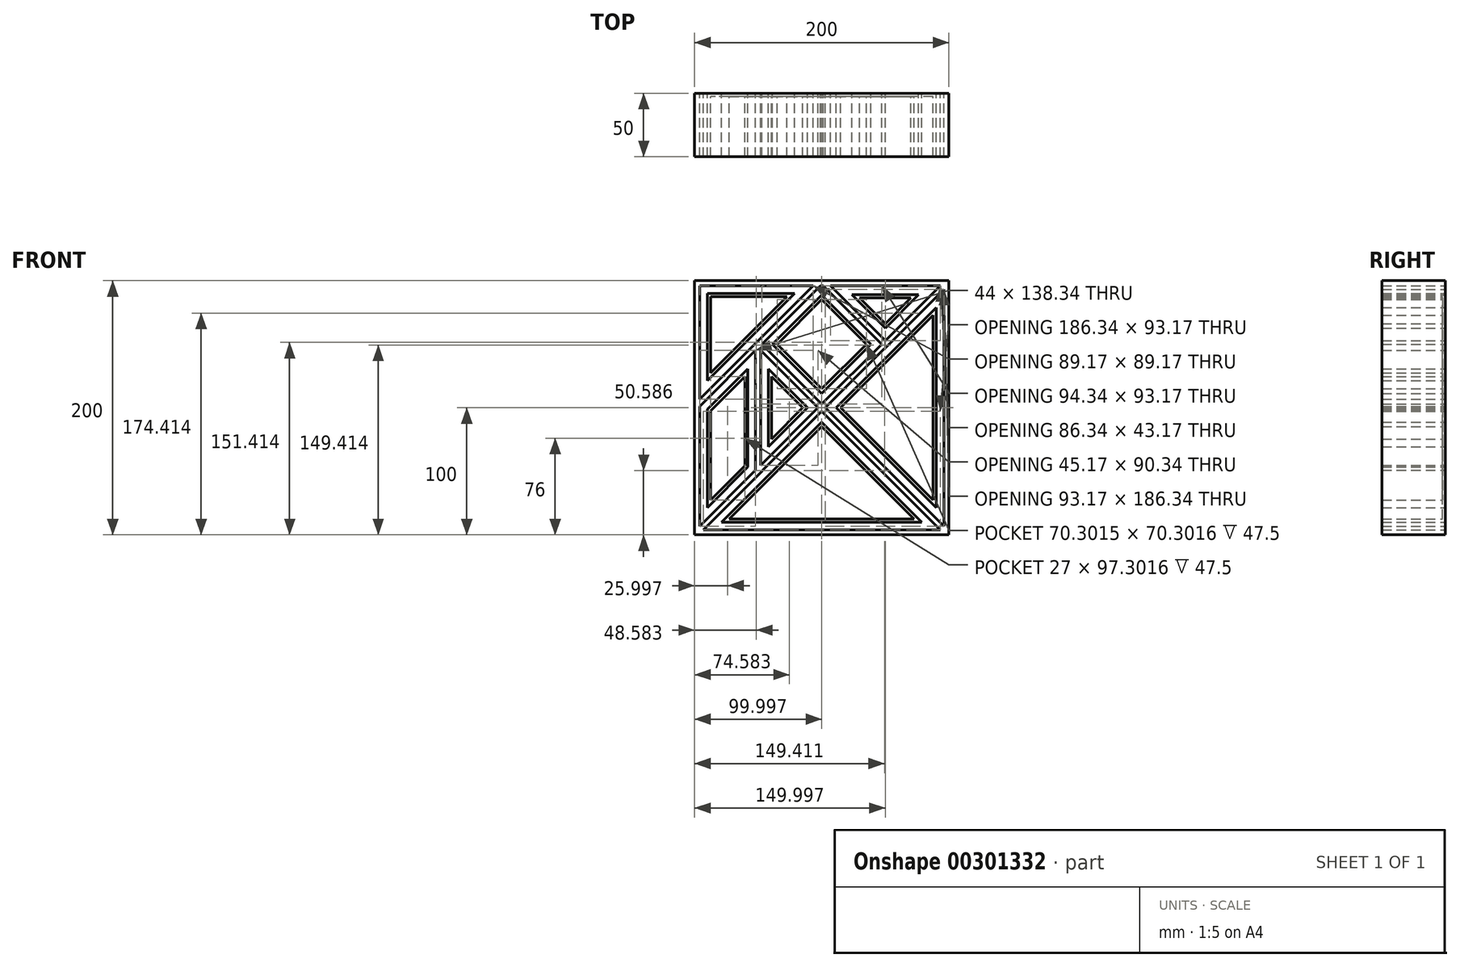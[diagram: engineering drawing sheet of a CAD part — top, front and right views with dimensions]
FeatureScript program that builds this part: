
annotation { "Feature Type Name" : "Feature", "Feature Type Description" : "" }
export const myFeature = defineFeature(function(context is Context, id is Id, definition is map)
    precondition{}
    {
        {
            var Q0;
            Q0=qCreatedBy(makeId("Front.planeOp"),FACE);
            var sketch = newSketch(context, id + "F0", { "sketchPlane" : qUnion([Q0])});
            skLineSegment(sketch, "E0.bottom", {"start": v(-112.27, 100) * mm, "end": v(87.73, 100) * mm});
            skLineSegment(sketch, "E0.top", {"start": v(-112.27, -100) * mm, "end": v(87.73, -100) * mm});
            skLineSegment(sketch, "E0.left", {"start": v(-112.27, 100) * mm, "end": v(-112.27, -100) * mm});
            skLineSegment(sketch, "E0.right", {"start": v(87.73, 100) * mm, "end": v(87.73, -100) * mm});
            skLineSegment(sketch, "E1", {"start": v(87.73, 100) * mm, "end": v(-108.27, -96) * mm, "construction": true});
            skLineSegment(sketch, "E2", {"start": v(-12.27, 100) * mm, "end": v(-112.27, 0) * mm, "construction": true});
            skLineSegment(sketch, "E3", {"start": v(-62.27, 50) * mm, "end": v(-62.27, -50) * mm, "construction": true});
            skLineSegment(sketch, "E4", {"start": v(-62.27, 50) * mm, "end": v(-12.27, 0) * mm, "construction": true});
            skPoint(sketch, "E4.endSnap0", {"position": v(-12.27, 0) * mm});
            skLineSegment(sketch, "E5", {"start": v(-12.27, 0) * mm, "end": v(83.73, -96) * mm, "construction": true});
            skLineSegment(sketch, "E6", {"start": v(-12.27, 100) * mm, "end": v(37.73, 50) * mm, "construction": true});
            skLineSegment(sketch, "E7.bottom", {"start": v(80.9, -96) * mm, "end": v(-105.44, -96) * mm});
            skLineSegment(sketch, "E7.top", {"start": v(80.9, 96) * mm, "end": v(-5.44, 96) * mm});
            skLineSegment(sketch, "E7.left", {"start": v(83.73, -93.17) * mm, "end": v(83.73, 93.17) * mm});
            skLineSegment(sketch, "E7.right", {"start": v(-108.27, -93.17) * mm, "end": v(-108.27, 1.17) * mm});
            skLineSegment(sketch, "E8", {"start": v(-19.1, 96) * mm, "end": v(-108.27, 6.83) * mm});
            skLineSegment(sketch, "E9", {"start": v(-108.27, 1.17) * mm, "end": v(-64.27, 45.17) * mm});
            skLineSegment(sketch, "E10", {"start": v(-64.27, 45.17) * mm, "end": v(-64.27, -49.17) * mm});
            skLineSegment(sketch, "E11", {"start": v(-64.27, -49.17) * mm, "end": v(-108.27, -93.17) * mm});
            skLineSegment(sketch, "E12", {"start": v(-105.44, -96) * mm, "end": v(-12.27, -2.83) * mm});
            skLineSegment(sketch, "E13", {"start": v(-12.27, -2.83) * mm, "end": v(80.9, -96) * mm});
            skLineSegment(sketch, "E14", {"start": v(83.73, 93.17) * mm, "end": v(-9.44, 0) * mm});
            skLineSegment(sketch, "E15", {"start": v(-9.44, 0) * mm, "end": v(83.73, -93.17) * mm});
            skLineSegment(sketch, "E16", {"start": v(-60.27, 45.17) * mm, "end": v(-60.27, -45.17) * mm});
            skLineSegment(sketch, "E17", {"start": v(-60.27, -45.17) * mm, "end": v(-15.1, 0) * mm});
            skLineSegment(sketch, "E18", {"start": v(-15.1, 0) * mm, "end": v(-60.27, 45.17) * mm});
            skLineSegment(sketch, "E19", {"start": v(-5.44, 96) * mm, "end": v(37.73, 52.83) * mm});
            skLineSegment(sketch, "E20", {"start": v(37.73, 52.83) * mm, "end": v(80.9, 96) * mm});
            skLineSegment(sketch, "E21", {"start": v(-13.44, 96) * mm, "end": v(-59.44, 50) * mm});
            skLineSegment(sketch, "E22", {"start": v(-59.44, 50) * mm, "end": v(-12.27, 2.83) * mm});
            skLineSegment(sketch, "E23", {"start": v(-12.27, 2.83) * mm, "end": v(34.9, 50) * mm});
            skLineSegment(sketch, "E24", {"start": v(34.9, 50) * mm, "end": v(-11.1, 96) * mm});
            skPoint(sketch, "E25.orphan", {"position": v(83.73, 96) * mm});
            skLineSegment(sketch, "E26.trimOffspring", {"start": v(-11.1, 96) * mm, "end": v(-13.44, 96) * mm});
            skLineSegment(sketch, "E27.trimOffspring", {"start": v(-19.1, 96) * mm, "end": v(-108.27, 96) * mm});
            skLineSegment(sketch, "E28.trimOffspring", {"start": v(-108.27, 6.83) * mm, "end": v(-108.27, 96) * mm});
            skPoint(sketch, "E29.orphan", {"position": v(-108.27, -96) * mm});
            skSolve(sketch);
        }
        {
            var Q0;
            Q0 = qSketchRegion(id + "F0", true);
            extrude(context, id + "F1", {"entities" : qUnion([Q0]), "depth" : 50 * mm});
        }
        {
            var Q0;
            Q0=qCreatedBy(makeId("Front.planeOp"),FACE);
            var sketch = newSketch(context, id + "F2", { "sketchPlane" : qUnion([Q0])});
            skLineSegment(sketch, "E30.0", {"start": v(81.73, 88.34) * mm, "end": v(-6.62, 0) * mm});
            skLineSegment(sketch, "E30.1", {"start": v(81.73, -88.34) * mm, "end": v(81.73, 88.34) * mm});
            skLineSegment(sketch, "E30.2", {"start": v(-6.62, 0) * mm, "end": v(81.73, -88.34) * mm});
            skLineSegment(sketch, "E31.0", {"start": v(77.73, 78.69) * mm, "end": v(-0.96, 0) * mm});
            skLineSegment(sketch, "E31.1", {"start": v(77.73, -78.69) * mm, "end": v(77.73, 78.69) * mm});
            skLineSegment(sketch, "E31.2", {"start": v(-0.96, 0) * mm, "end": v(77.73, -78.69) * mm});
            skLineSegment(sketch, "E32.0", {"start": v(-0.62, 94) * mm, "end": v(37.73, 55.66) * mm});
            skLineSegment(sketch, "E32.1", {"start": v(76.07, 94) * mm, "end": v(-0.62, 94) * mm});
            skLineSegment(sketch, "E32.2", {"start": v(37.73, 55.66) * mm, "end": v(76.07, 94) * mm});
            skLineSegment(sketch, "E33.0", {"start": v(11.46, 89) * mm, "end": v(37.73, 62.73) * mm});
            skLineSegment(sketch, "E33.1", {"start": v(64, 89) * mm, "end": v(11.46, 89) * mm});
            skLineSegment(sketch, "E33.2", {"start": v(37.73, 62.73) * mm, "end": v(64, 89) * mm});
            skLineSegment(sketch, "E34.0", {"start": v(-100.62, -94) * mm, "end": v(-12.27, -5.66) * mm});
            skLineSegment(sketch, "E34.1", {"start": v(76.07, -94) * mm, "end": v(-100.62, -94) * mm});
            skLineSegment(sketch, "E34.2", {"start": v(-12.27, -5.66) * mm, "end": v(76.07, -94) * mm});
            skLineSegment(sketch, "E35.0", {"start": v(-90.96, -90) * mm, "end": v(-12.27, -11.31) * mm});
            skLineSegment(sketch, "E35.1", {"start": v(66.41, -90) * mm, "end": v(-90.96, -90) * mm});
            skLineSegment(sketch, "E35.2", {"start": v(-12.27, -11.31) * mm, "end": v(66.41, -90) * mm});
            skLineSegment(sketch, "E36.0", {"start": v(-106.27, 0.34) * mm, "end": v(-66.27, 40.34) * mm});
            skLineSegment(sketch, "E36.1", {"start": v(-106.27, -88.34) * mm, "end": v(-106.27, 0.34) * mm});
            skLineSegment(sketch, "E36.2", {"start": v(-66.27, -48.34) * mm, "end": v(-106.27, -88.34) * mm});
            skLineSegment(sketch, "E36.3", {"start": v(-66.27, 40.34) * mm, "end": v(-66.27, -48.34) * mm});
            skLineSegment(sketch, "E37.0", {"start": v(-102.27, -78.69) * mm, "end": v(-102.27, -1.31) * mm});
            skLineSegment(sketch, "E37.1", {"start": v(-70.27, -46.69) * mm, "end": v(-102.27, -78.69) * mm});
            skLineSegment(sketch, "E37.2", {"start": v(-70.27, 30.69) * mm, "end": v(-70.27, -46.69) * mm});
            skLineSegment(sketch, "E37.3", {"start": v(-102.27, -1.31) * mm, "end": v(-70.27, 30.69) * mm});
            skLineSegment(sketch, "E38.0", {"start": v(-23.93, 94) * mm, "end": v(-106.27, 11.66) * mm});
            skLineSegment(sketch, "E38.1", {"start": v(-23.93, 94) * mm, "end": v(-106.27, 94) * mm});
            skLineSegment(sketch, "E38.2", {"start": v(-106.27, 11.66) * mm, "end": v(-106.27, 94) * mm});
            skLineSegment(sketch, "E39.0", {"start": v(-102.27, 21.31) * mm, "end": v(-102.27, 90) * mm});
            skLineSegment(sketch, "E39.1", {"start": v(-33.59, 90) * mm, "end": v(-102.27, 21.31) * mm});
            skLineSegment(sketch, "E39.2", {"start": v(-33.59, 90) * mm, "end": v(-102.27, 90) * mm});
            skLineSegment(sketch, "E40.0", {"start": v(-58.27, 40.34) * mm, "end": v(-58.27, -40.34) * mm});
            skLineSegment(sketch, "E40.1", {"start": v(-17.93, 0) * mm, "end": v(-58.27, 40.34) * mm});
            skLineSegment(sketch, "E40.2", {"start": v(-58.27, -40.34) * mm, "end": v(-17.93, 0) * mm});
            skLineSegment(sketch, "E41.0", {"start": v(-54.27, 30.69) * mm, "end": v(-54.27, -30.69) * mm});
            skLineSegment(sketch, "E41.1", {"start": v(-23.59, 0) * mm, "end": v(-54.27, 30.69) * mm});
            skLineSegment(sketch, "E41.2", {"start": v(-54.27, -30.69) * mm, "end": v(-23.59, 0) * mm});
            skLineSegment(sketch, "E42.0", {"start": v(32.07, 50) * mm, "end": v(-12.27, 94.34) * mm});
            skLineSegment(sketch, "E42.1", {"start": v(-12.27, 5.66) * mm, "end": v(32.07, 50) * mm});
            skLineSegment(sketch, "E42.2", {"start": v(-56.62, 50) * mm, "end": v(-12.27, 5.66) * mm});
            skLineSegment(sketch, "E42.3", {"start": v(-12.27, 94.34) * mm, "end": v(-56.62, 50) * mm});
            skLineSegment(sketch, "E43.0", {"start": v(-12.27, 88.69) * mm, "end": v(-50.96, 50) * mm});
            skLineSegment(sketch, "E43.1", {"start": v(26.41, 50) * mm, "end": v(-12.27, 88.69) * mm});
            skLineSegment(sketch, "E43.2", {"start": v(-12.27, 11.31) * mm, "end": v(26.41, 50) * mm});
            skLineSegment(sketch, "E43.3", {"start": v(-50.96, 50) * mm, "end": v(-12.27, 11.31) * mm});
            skSolve(sketch);
        }
        {
            var Q0;
            Q0=makeQuery(id+"F2.imprint","IMPRINT",FACE,{"disambiguationData":[TD([[makeQuery(id+"F2.imprint","IMPRINT",EDGE,{"derivedFrom":sQuery(id+"F2.wireOp",EDGE,"E31.0")}),1.0]])]});
            var Q1;
            Q1=makeQuery(id+"F2.imprint","IMPRINT",FACE,{"disambiguationData":[TD([[makeQuery(id+"F2.imprint","IMPRINT",EDGE,{"derivedFrom":sQuery(id+"F2.wireOp",EDGE,"E35.0")}),-1.0]])]});
            var Q2;
            Q2=makeQuery(id+"F2.imprint","IMPRINT",FACE,{"disambiguationData":[TD([[makeQuery(id+"F2.imprint","IMPRINT",EDGE,{"derivedFrom":sQuery(id+"F2.wireOp",EDGE,"E43.0")}),1.0]])]});
            var Q3;
            Q3=makeQuery(id+"F2.imprint","IMPRINT",FACE,{"disambiguationData":[TD([[makeQuery(id+"F2.imprint","IMPRINT",EDGE,{"derivedFrom":sQuery(id+"F2.wireOp",EDGE,"E41.0")}),1.0]])]});
            var Q4;
            Q4=makeQuery(id+"F2.imprint","IMPRINT",FACE,{"disambiguationData":[TD([[makeQuery(id+"F2.imprint","IMPRINT",EDGE,{"derivedFrom":sQuery(id+"F2.wireOp",EDGE,"E37.0")}),-1.0]])]});
            var Q5;
            Q5=makeQuery(id+"F2.imprint","IMPRINT",FACE,{"disambiguationData":[TD([[makeQuery(id+"F2.imprint","IMPRINT",EDGE,{"derivedFrom":sQuery(id+"F2.wireOp",EDGE,"E39.0")}),-1.0]])]});
            var Q6;
            Q6=makeQuery(id+"F2.imprint","IMPRINT",FACE,{"disambiguationData":[TD([[makeQuery(id+"F2.imprint","IMPRINT",EDGE,{"derivedFrom":sQuery(id+"F2.wireOp",EDGE,"E33.0")}),1.0]])]});
            extrude(context, id + "F3", {"entities" : qUnion([Q0, Q1, Q2, Q3, Q4, Q5, Q6]), "depth" : 50 * mm});
        }
        {
            var Q0;
            Q0=makeQuery(id+"F3.opExtrude","CAP_FACE",FACE,{"disambiguationData":[OSD([sQuery(id+"F2.wireOp",EDGE,"E37.0"),sQuery(id+"F2.wireOp",EDGE,"E37.1"),sQuery(id+"F2.wireOp",EDGE,"E37.2"),sQuery(id+"F2.wireOp",EDGE,"E37.3")])],"isStart":false});
            var Q1;
            Q1=makeQuery(id+"F3.opExtrude","CAP_FACE",FACE,{"disambiguationData":[OSD([sQuery(id+"F2.wireOp",EDGE,"E39.0"),sQuery(id+"F2.wireOp",EDGE,"E39.1"),sQuery(id+"F2.wireOp",EDGE,"E39.2")])],"isStart":false});
            var Q2;
            Q2=makeQuery(id+"F3.opExtrude","CAP_FACE",FACE,{"disambiguationData":[OSD([sQuery(id+"F2.wireOp",EDGE,"E35.0"),sQuery(id+"F2.wireOp",EDGE,"E35.1"),sQuery(id+"F2.wireOp",EDGE,"E35.2")])],"isStart":false});
            var Q3;
            Q3=makeQuery(id+"F3.opExtrude","CAP_FACE",FACE,{"disambiguationData":[OSD([sQuery(id+"F2.wireOp",EDGE,"E41.0"),sQuery(id+"F2.wireOp",EDGE,"E41.1"),sQuery(id+"F2.wireOp",EDGE,"E41.2")])],"isStart":false});
            var Q4;
            Q4=makeQuery(id+"F3.opExtrude","CAP_FACE",FACE,{"disambiguationData":[OSD([sQuery(id+"F2.wireOp",EDGE,"E43.0"),sQuery(id+"F2.wireOp",EDGE,"E43.1"),sQuery(id+"F2.wireOp",EDGE,"E43.2"),sQuery(id+"F2.wireOp",EDGE,"E43.3")])],"isStart":false});
            var Q5;
            Q5=makeQuery(id+"F3.opExtrude","CAP_FACE",FACE,{"disambiguationData":[OSD([sQuery(id+"F2.wireOp",EDGE,"E33.0"),sQuery(id+"F2.wireOp",EDGE,"E33.1"),sQuery(id+"F2.wireOp",EDGE,"E33.2")])],"isStart":false});
            var Q6;
            Q6=makeQuery(id+"F3.opExtrude","CAP_FACE",FACE,{"disambiguationData":[OSD([sQuery(id+"F2.wireOp",EDGE,"E31.0"),sQuery(id+"F2.wireOp",EDGE,"E31.1"),sQuery(id+"F2.wireOp",EDGE,"E31.2")])],"isStart":false});
            shell(context, id + "F4", {"entities" : qUnion([Q0, Q1, Q2, Q3, Q4, Q5, Q6]), "thickness" : 2.5 * mm});
        }
    });
